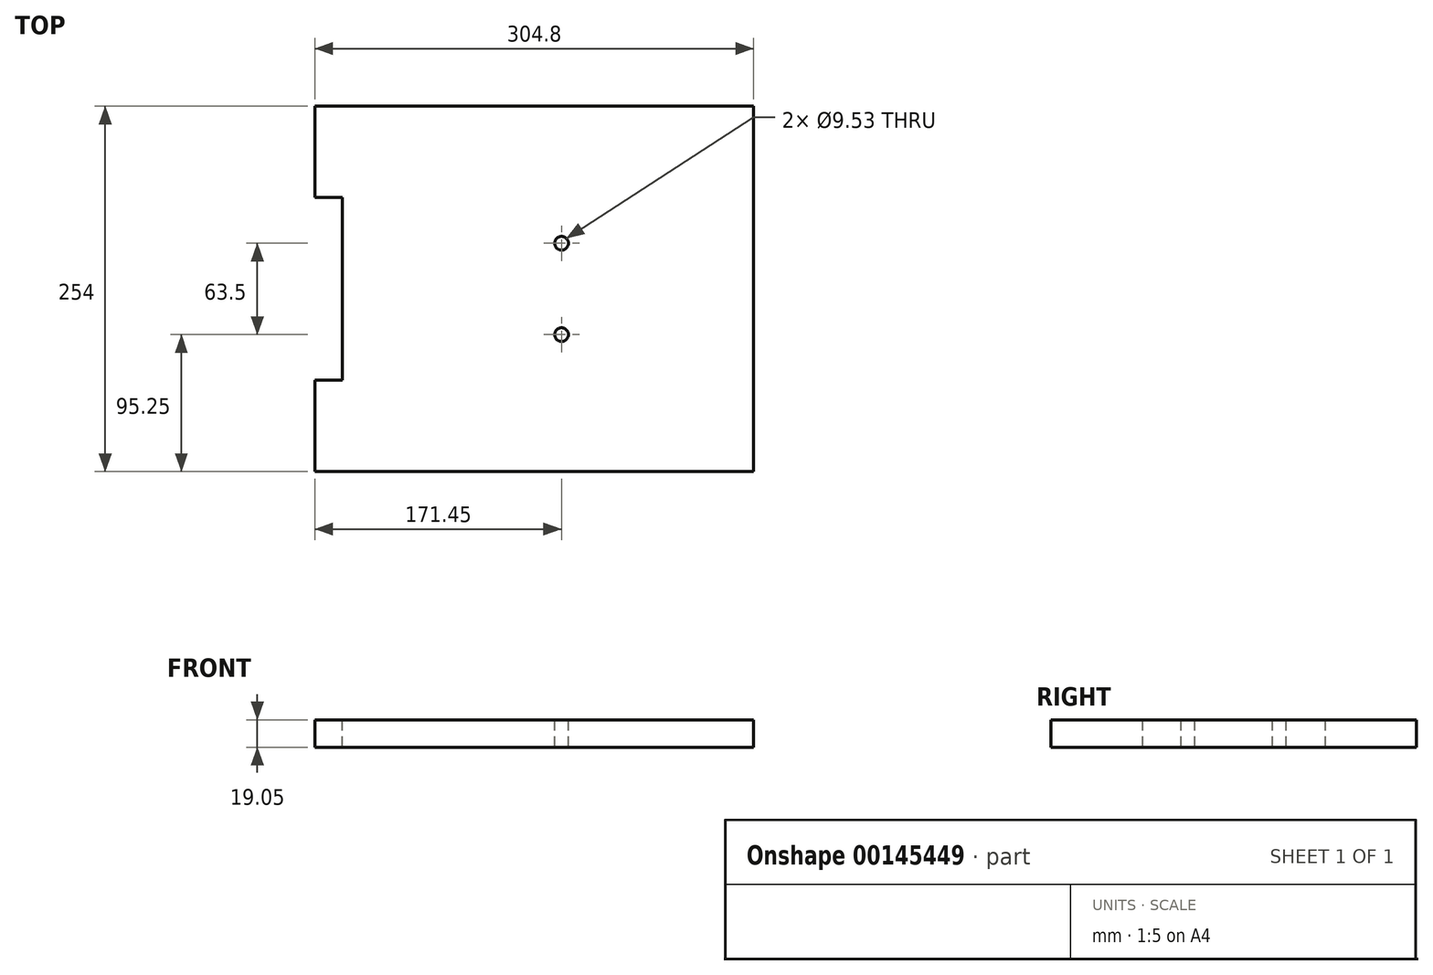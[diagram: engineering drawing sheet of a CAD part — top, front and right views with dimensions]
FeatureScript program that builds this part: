
annotation { "Feature Type Name" : "Feature", "Feature Type Description" : "" }
export const myFeature = defineFeature(function(context is Context, id is Id, definition is map)
    precondition{}
    {
        {
            var Q0;
            Q0=qCreatedBy(makeId("Top.planeOp"),FACE);
            var sketch = newSketch(context, id + "F0", { "sketchPlane" : qUnion([Q0])});
            skLineSegment(sketch, "E0.bottom", {"start": v(-152.4, 127) * mm, "end": v(152.4, 127) * mm});
            skLineSegment(sketch, "E0.top", {"start": v(-152.4, -127) * mm, "end": v(152.4, -127) * mm});
            skLineSegment(sketch, "E0.left", {"start": v(-152.4, 127) * mm, "end": v(-152.4, -127) * mm});
            skLineSegment(sketch, "E0.right", {"start": v(152.4, 127) * mm, "end": v(152.4, -127) * mm});
            skPoint(sketch, "E0.middle", {"position": v(0, 0) * mm});
            skSolve(sketch);
        }
        {
            var Q0;
            Q0 = qSketchRegion(id + "F0", true);
            extrude(context, id + "F1", {"entities" : qUnion([Q0]), "depth" : 19.05 * mm});
        }
        {
            var Q0;
            Q0=makeQuery(id+"F1.opExtrude","CAP_FACE",FACE,{"disambiguationData":[OSD([sQuery(id+"F0.wireOp",EDGE,"E0.bottom"),sQuery(id+"F0.wireOp",EDGE,"E0.top"),sQuery(id+"F0.wireOp",EDGE,"E0.left"),sQuery(id+"F0.wireOp",EDGE,"E0.right")])],"isStart":false});
            var sketch = newSketch(context, id + "F2", { "sketchPlane" : qUnion([Q0])});
            skLineSegment(sketch, "E1.bottom", {"start": v(-171.45, 63.5) * mm, "end": v(-133.35, 63.5) * mm});
            skLineSegment(sketch, "E1.top", {"start": v(-171.45, -63.5) * mm, "end": v(-133.35, -63.5) * mm});
            skLineSegment(sketch, "E1.left", {"start": v(-171.45, 63.5) * mm, "end": v(-171.45, -63.5) * mm});
            skLineSegment(sketch, "E1.right", {"start": v(-133.35, 63.5) * mm, "end": v(-133.35, -63.5) * mm});
            skPoint(sketch, "E1.middle", {"position": v(-152.4, 0) * mm});
            skSolve(sketch);
        }
        {
            var Q0;
            Q0 = qSketchRegion(id + "F2", true);
            extrude(context, id + "F3", {"entities" : qUnion([Q0]), "operationType" : NewBodyOperationType.REMOVE, "endBound" : BoundingType.THROUGH_ALL, "oppositeDirection" : true, "depth" : 25.4 * mm});
        }
        {
            var Q0;
            Q0=makeQuery(id+"F1.opExtrude","CAP_FACE",FACE,{"disambiguationData":[OSD([sQuery(id+"F0.wireOp",EDGE,"E0.bottom"),sQuery(id+"F0.wireOp",EDGE,"E0.top"),sQuery(id+"F0.wireOp",EDGE,"E0.left"),sQuery(id+"F0.wireOp",EDGE,"E0.right")])],"isStart":false});
            var sketch = newSketch(context, id + "F4", { "sketchPlane" : qUnion([Q0])});
            skLineSegment(sketch, "E2", {"start": v(-133.35, 0) * mm, "end": v(0, 0) * mm, "construction": true});
            skCircle(sketch, "E3", {"center": v(19.05, 31.75) * mm, "radius": 4.76 * mm});
            skCircle(sketch, "E4", {"center": v(19.05, -31.75) * mm, "radius": 4.76 * mm});
            skSolve(sketch);
        }
        {
            var Q0;
            Q0 = qSketchRegion(id + "F4", true);
            extrude(context, id + "F5", {"entities" : qUnion([Q0]), "operationType" : NewBodyOperationType.REMOVE, "endBound" : BoundingType.THROUGH_ALL, "oppositeDirection" : true, "depth" : 25.4 * mm});
        }
    });
